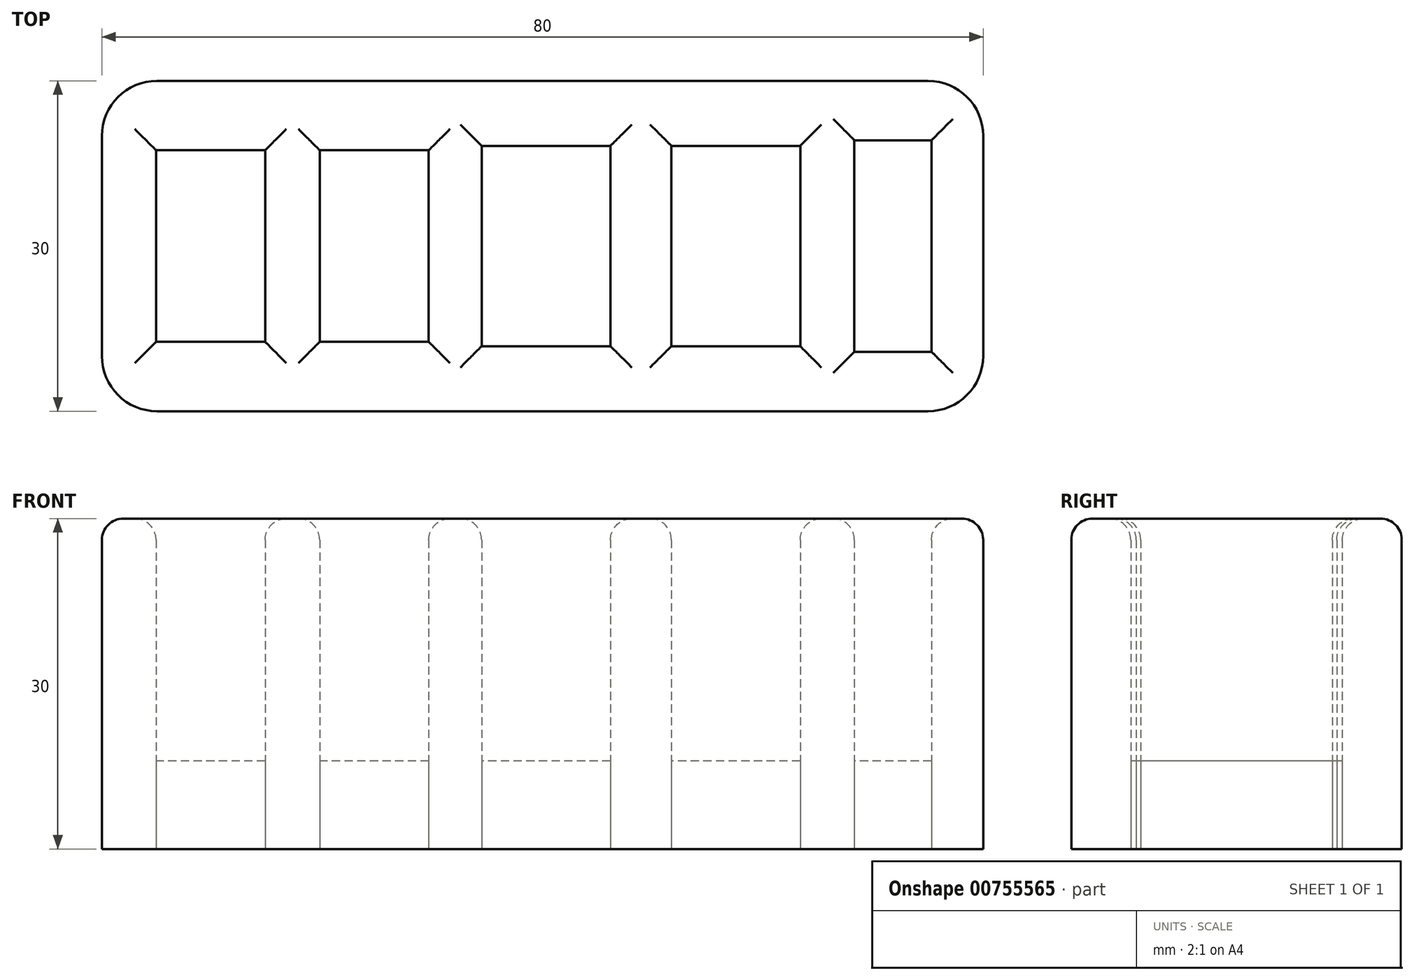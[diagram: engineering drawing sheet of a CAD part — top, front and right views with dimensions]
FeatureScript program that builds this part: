
annotation { "Feature Type Name" : "Feature", "Feature Type Description" : "" }
export const myFeature = defineFeature(function(context is Context, id is Id, definition is map)
    precondition{}
    {
        {
            var Q0;
            Q0=qCreatedBy(makeId("Top.planeOp"),FACE);
            var sketch = newSketch(context, id + "F0", { "sketchPlane" : qUnion([Q0])});
            skLineSegment(sketch, "E0.bottom", {"start": v(40, 15) * mm, "end": v(-40, 15) * mm});
            skLineSegment(sketch, "E0.top", {"start": v(40, -15) * mm, "end": v(-40, -15) * mm});
            skLineSegment(sketch, "E0.left", {"start": v(40, 15) * mm, "end": v(40, -15) * mm});
            skLineSegment(sketch, "E0.right", {"start": v(-40, 15) * mm, "end": v(-40, -15) * mm});
            skPoint(sketch, "E0.middle", {"position": v(0, 0) * mm});
            skLineSegment(sketch, "E1.bottom", {"start": v(-25.18, 8.7) * mm, "end": v(-35.08, 8.7) * mm});
            skLineSegment(sketch, "E1.top", {"start": v(-25.18, -8.7) * mm, "end": v(-35.08, -8.7) * mm});
            skLineSegment(sketch, "E1.left", {"start": v(-25.18, 8.7) * mm, "end": v(-25.18, -8.7) * mm});
            skLineSegment(sketch, "E1.right", {"start": v(-35.08, 8.7) * mm, "end": v(-35.08, -8.7) * mm});
            skPoint(sketch, "E1.middle", {"position": v(-30.13, 0) * mm});
            skLineSegment(sketch, "E2.bottom", {"start": v(-10.33, 8.7) * mm, "end": v(-20.23, 8.7) * mm});
            skLineSegment(sketch, "E2.top", {"start": v(-10.33, -8.7) * mm, "end": v(-20.23, -8.7) * mm});
            skLineSegment(sketch, "E2.left", {"start": v(-10.33, 8.7) * mm, "end": v(-10.33, -8.7) * mm});
            skLineSegment(sketch, "E2.right", {"start": v(-20.23, 8.7) * mm, "end": v(-20.23, -8.7) * mm});
            skPoint(sketch, "E2.middle", {"position": v(-15.28, 0) * mm});
            skPoint(sketch, "E2.cornerSnap0", {"position": v(-30.13, 8.7) * mm});
            skLineSegment(sketch, "E3.bottom", {"start": v(23.4, 9.1) * mm, "end": v(11.7, 9.1) * mm});
            skLineSegment(sketch, "E3.top", {"start": v(23.4, -9.1) * mm, "end": v(11.7, -9.1) * mm});
            skLineSegment(sketch, "E3.left", {"start": v(23.4, 9.1) * mm, "end": v(23.4, -9.1) * mm});
            skLineSegment(sketch, "E3.right", {"start": v(11.7, 9.1) * mm, "end": v(11.7, -9.1) * mm});
            skPoint(sketch, "E3.middle", {"position": v(17.54, 0) * mm});
            skLineSegment(sketch, "E4.bottom", {"start": v(35.31, 9.6) * mm, "end": v(28.31, 9.6) * mm});
            skLineSegment(sketch, "E4.top", {"start": v(35.31, -9.6) * mm, "end": v(28.31, -9.6) * mm});
            skLineSegment(sketch, "E4.left", {"start": v(35.31, 9.6) * mm, "end": v(35.31, -9.6) * mm});
            skLineSegment(sketch, "E4.right", {"start": v(28.31, 9.6) * mm, "end": v(28.31, -9.6) * mm});
            skPoint(sketch, "E4.middle", {"position": v(31.81, 0) * mm});
            skLineSegment(sketch, "E5.bottom", {"start": v(6.17, 9.1) * mm, "end": v(-5.53, 9.1) * mm});
            skLineSegment(sketch, "E5.top", {"start": v(6.17, -9.1) * mm, "end": v(-5.53, -9.1) * mm});
            skLineSegment(sketch, "E5.left", {"start": v(6.17, 9.1) * mm, "end": v(6.17, -9.1) * mm});
            skLineSegment(sketch, "E5.right", {"start": v(-5.53, 9.1) * mm, "end": v(-5.53, -9.1) * mm});
            skPoint(sketch, "E5.middle", {"position": v(0.32, 0) * mm});
            skLineSegment(sketch, "E6", {"start": v(0, 9.1) * mm, "end": v(0, -9.1) * mm, "construction": true});
            skPoint(sketch, "E6.startSnap0", {"position": v(0.32, 9.1) * mm});
            skLineSegment(sketch, "E7", {"start": v(-5.53, -9.1) * mm, "end": v(-5.53, -15) * mm, "construction": true});
            skSolve(sketch);
        }
        {
            var Q0;
            Q0=makeQuery(id+"F0.imprint","IMPRINT",FACE,{"disambiguationData":[TD([[makeQuery(id+"F0.imprint","IMPRINT",EDGE,{"derivedFrom":sQuery(id+"F0.wireOp",EDGE,"E1.bottom")}),1.0]])]});
            var Q1;
            Q1=makeQuery(id+"F0.imprint","IMPRINT",FACE,{"disambiguationData":[TD([[makeQuery(id+"F0.imprint","IMPRINT",EDGE,{"derivedFrom":sQuery(id+"F0.wireOp",EDGE,"E2.bottom")}),1.0]])]});
            var Q2;
            Q2=makeQuery(id+"F0.imprint","IMPRINT",FACE,{"disambiguationData":[TD([[makeQuery(id+"F0.imprint","IMPRINT",EDGE,{"derivedFrom":sQuery(id+"F0.wireOp",EDGE,"E5.bottom")}),1.0]])]});
            var Q3;
            Q3=makeQuery(id+"F0.imprint","IMPRINT",FACE,{"disambiguationData":[TD([[makeQuery(id+"F0.imprint","IMPRINT",EDGE,{"derivedFrom":sQuery(id+"F0.wireOp",EDGE,"E3.bottom")}),1.0]])]});
            var Q4;
            Q4=makeQuery(id+"F0.imprint","IMPRINT",FACE,{"disambiguationData":[TD([[makeQuery(id+"F0.imprint","IMPRINT",EDGE,{"derivedFrom":sQuery(id+"F0.wireOp",EDGE,"E4.bottom")}),1.0]])]});
            extrude(context, id + "F1", {"entities" : qUnion([Q0, Q1, Q2, Q3, Q4]), "depth" : 8 * mm, "offsetDistance" : 25 * mm});
        }
        {
            var Q0;
            Q0=makeQuery(id+"F0.imprint","IMPRINT",FACE,{"disambiguationData":[TD([[makeQuery(id+"F0.imprint","IMPRINT",EDGE,{"derivedFrom":sQuery(id+"F0.wireOp",EDGE,"E0.bottom")}),1.0]])]});
            extrude(context, id + "F2", {"entities" : qUnion([Q0]), "depth" : 30 * mm, "offsetDistance" : 25 * mm});
        }
        {
            var Q0;
            Q0=makeQuery(id+"F2.opExtrude","CAP_FACE",FACE,{"disambiguationData":[OSD([sQuery(id+"F0.wireOp",EDGE,"E0.bottom"),sQuery(id+"F0.wireOp",EDGE,"E0.top"),sQuery(id+"F0.wireOp",EDGE,"E0.left"),sQuery(id+"F0.wireOp",EDGE,"E0.right"),sQuery(id+"F0.wireOp",EDGE,"E1.bottom"),sQuery(id+"F0.wireOp",EDGE,"E1.top"),sQuery(id+"F0.wireOp",EDGE,"E1.left"),sQuery(id+"F0.wireOp",EDGE,"E1.right"),sQuery(id+"F0.wireOp",EDGE,"E2.bottom"),sQuery(id+"F0.wireOp",EDGE,"E2.top"),sQuery(id+"F0.wireOp",EDGE,"E2.left"),sQuery(id+"F0.wireOp",EDGE,"E2.right"),sQuery(id+"F0.wireOp",EDGE,"E3.bottom"),sQuery(id+"F0.wireOp",EDGE,"E3.top"),sQuery(id+"F0.wireOp",EDGE,"E3.left"),sQuery(id+"F0.wireOp",EDGE,"E3.right"),sQuery(id+"F0.wireOp",EDGE,"E4.bottom"),sQuery(id+"F0.wireOp",EDGE,"E4.top"),sQuery(id+"F0.wireOp",EDGE,"E4.left"),sQuery(id+"F0.wireOp",EDGE,"E4.right"),sQuery(id+"F0.wireOp",EDGE,"E5.bottom"),sQuery(id+"F0.wireOp",EDGE,"E5.top"),sQuery(id+"F0.wireOp",EDGE,"E5.left"),sQuery(id+"F0.wireOp",EDGE,"E5.right")])],"isStart":false});
            fillet(context, id + "F3", {"entities" : qUnion([Q0]), "radius" : 1.93 * mm, "tangentPropagation" : true, "allowEdgeOverflow" : false});
        }
        {
            var Q0;
            Q0=makeQuery(id+"F2.opExtrude","SWEPT_EDGE",EDGE,{"disambiguationData":[OSD([sQuery(id+"F0.wireOp",EDGE,"E0.top"),sQuery(id+"F0.wireOp",EDGE,"E0.left")])]});
            var Q1;
            Q1=makeQuery(id+"F2.opExtrude","SWEPT_EDGE",EDGE,{"disambiguationData":[OSD([sQuery(id+"F0.wireOp",EDGE,"E0.bottom"),sQuery(id+"F0.wireOp",EDGE,"E0.left")])]});
            var Q2;
            Q2=makeQuery(id+"F2.opExtrude","SWEPT_EDGE",EDGE,{"disambiguationData":[OSD([sQuery(id+"F0.wireOp",EDGE,"E0.bottom"),sQuery(id+"F0.wireOp",EDGE,"E0.right")])]});
            var Q3;
            Q3=makeQuery(id+"F2.opExtrude","SWEPT_EDGE",EDGE,{"disambiguationData":[OSD([sQuery(id+"F0.wireOp",EDGE,"E0.top"),sQuery(id+"F0.wireOp",EDGE,"E0.right")])]});
            fillet(context, id + "F4", {"entities" : qUnion([Q0, Q1, Q2, Q3]), "radius" : 5 * mm, "tangentPropagation" : true, "allowEdgeOverflow" : false});
        }
    });
